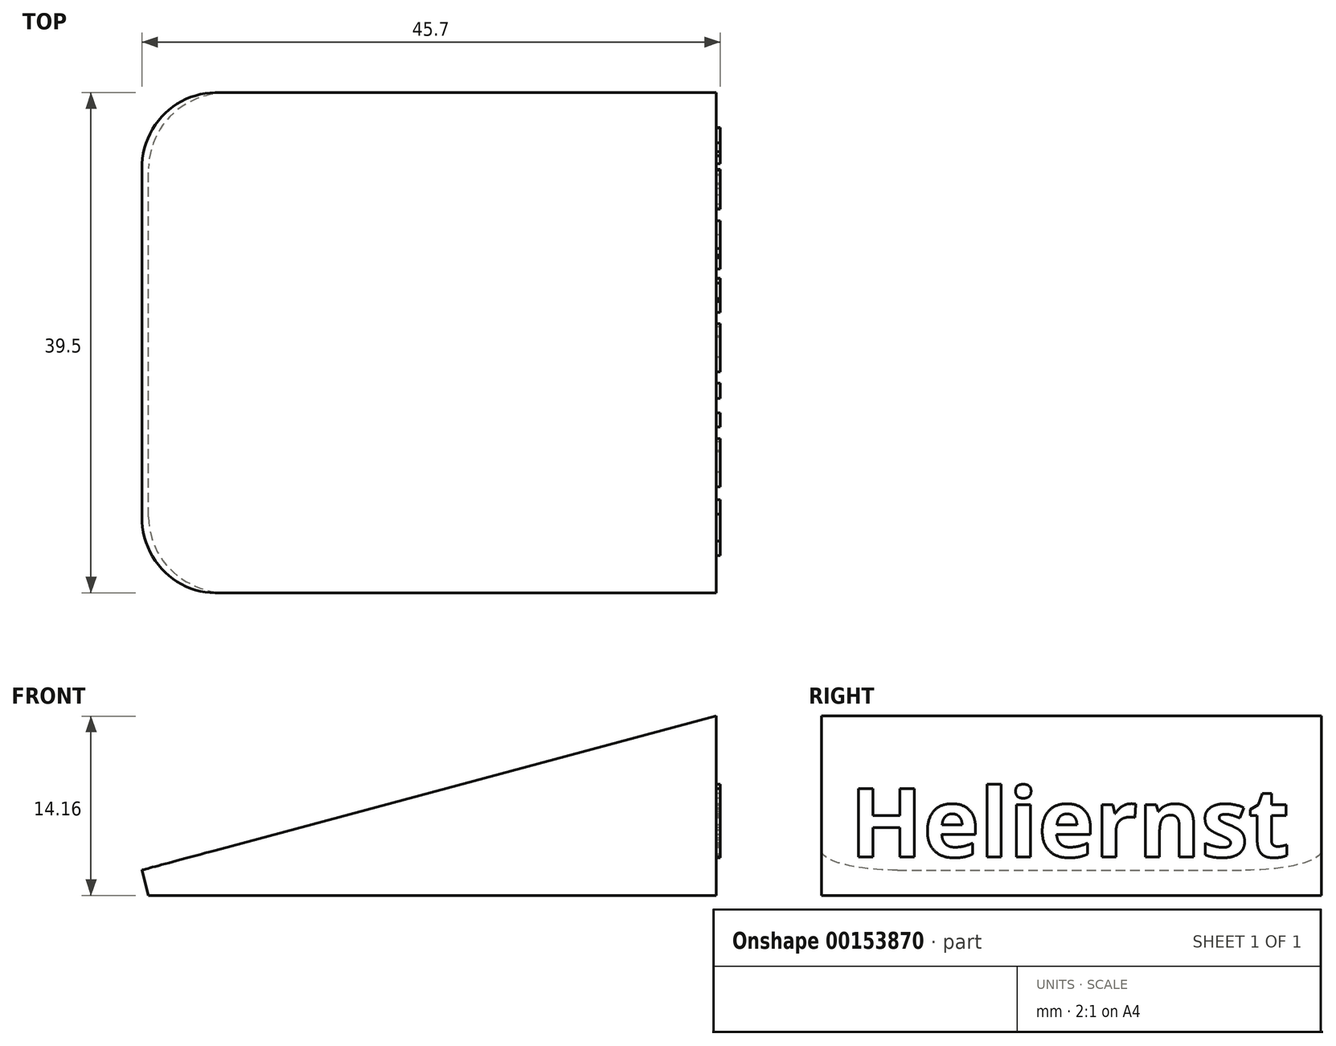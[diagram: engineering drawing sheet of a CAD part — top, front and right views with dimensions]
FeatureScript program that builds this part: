
annotation { "Feature Type Name" : "Feature", "Feature Type Description" : "" }
export const myFeature = defineFeature(function(context is Context, id is Id, definition is map)
    precondition{}
    {
        {
            var Q0;
            Q0=qCreatedBy(makeId("Right.planeOp"),FACE);
            var sketch = newSketch(context, id + "F0", { "sketchPlane" : qUnion([Q0])});
            skLineSegment(sketch, "E0", {"start": v(0, 0) * mm, "end": v(45.4, 0) * mm});
            skLineSegment(sketch, "E1", {"start": v(45.4, 0) * mm, "end": v(45.4, 14.16) * mm});
            skLineSegment(sketch, "E2", {"start": v(45.4, 14.16) * mm, "end": v(0, 2) * mm});
            skLineSegment(sketch, "E3", {"start": v(0, 2) * mm, "end": v(0, 0) * mm});
            skSolve(sketch);
        }
        {
            var Q0;
            Q0=qSketchRegion(id+"F0",true);
            extrude(context, id + "F1", {"entities" : qUnion([Q0]), "depth" : 39.5 * mm});
        }
        {
            var Q0;
            Q0=makeQuery(id+"F1.opExtrude","SWEPT_BODY",BODY,{"disambiguationData":[OSD([sQuery(id+"F0.wireOp",EDGE,"E0"),sQuery(id+"F0.wireOp",EDGE,"E1"),sQuery(id+"F0.wireOp",EDGE,"E2")])]});
            transform(context, id + "F2", {"entities" : qUnion([Q0]), "transformType" : TransformType.TRANSLATION_3D, "dx" : -10.75 * mm, "dy" : -78 * mm, "dz" : 41.5 * mm, "makeCopy" : true});
        }
        {
            var Q0;
            Q0=makeQuery(id+"F2.opPattern","COPY",BODY,{"derivedFrom":makeQuery(id+"F1.opExtrude","SWEPT_BODY",BODY,{"disambiguationData":[OSD([sQuery(id+"F0.wireOp",EDGE,"E0"),sQuery(id+"F0.wireOp",EDGE,"E1"),sQuery(id+"F0.wireOp",EDGE,"E2")])]}),"instanceName":"1"});
            deleteBodies(context, id + "F3", {"entities" : qUnion([Q0])});
        }
        {
            var Q0;
            Q0=makeQuery(id+"F1.opExtrude","SWEPT_BODY",BODY,{"disambiguationData":[OSD([sQuery(id+"F0.wireOp",EDGE,"E0"),sQuery(id+"F0.wireOp",EDGE,"E1"),sQuery(id+"F0.wireOp",EDGE,"E2")])]});
            var Q1;
            Q1=makeQuery(id+"F1.opExtrude","CAP_EDGE",EDGE,{"disambiguationData":[OSD([sQuery(id+"F0.wireOp",EDGE,"E1")])],"isStart":true});
            transform(context, id + "F4", {"entities" : qUnion([Q0]), "transformType" : TransformType.ROTATION, "transformAxis" : qUnion([Q1]), "angle" : 90 * degree, "makeCopy" : false});
        }
        {
            var Q0;
            Q0=makeQuery(id+"F1.opExtrude","SWEPT_BODY",BODY,{"disambiguationData":[OSD([sQuery(id+"F0.wireOp",EDGE,"E0"),sQuery(id+"F0.wireOp",EDGE,"E1"),sQuery(id+"F0.wireOp",EDGE,"E2")])]});
            var Q1;
            Q1=makeQuery(id+"F1.opExtrude","CAP_EDGE",EDGE,{"disambiguationData":[OSD([sQuery(id+"F0.wireOp",EDGE,"E1")])],"isStart":true});
            transform(context, id + "F5", {"entities" : qUnion([Q0]), "transformType" : TransformType.ROTATION, "transformAxis" : qUnion([Q1]), "angle" : 180 * degree, "makeCopy" : false});
        }
        {
            var Q0;
            Q0=makeQuery(id+"F1.opExtrude","SWEPT_FACE",FACE,{"disambiguationData":[OSD([sQuery(id+"F0.wireOp",EDGE,"E1")])]});
            var sketch = newSketch(context, id + "F6", { "sketchPlane" : qUnion([Q0])});
            skText(sketch, "E4", { "text": "Heliernst", "fontName": "OpenSans-Bold.ttf"});
            skLineSegment(sketch, "E5", {"start": v(25.65, 14.16) * mm, "end": v(25.65, -4.48) * mm, "construction": true});
            const initialGuessF6  = {"E4": [0.00815, 0.00304, 1, 0, 0.00544]};
            skSetInitialGuess(sketch, initialGuessF6);
            skSolve(sketch);
        }
        {
            var Q0;
            Q0 = qSketchRegion(id + "F6", true);
            extrude(context, id + "F7", {"entities" : qUnion([Q0]), "operationType" : NewBodyOperationType.ADD, "depth" : 0.3 * mm});
        }
        {
            var Q0;
            Q0=makeQuery(id+"F1.opExtrude","SWEPT_FACE",FACE,{"disambiguationData":[OSD([sQuery(id+"F0.wireOp",EDGE,"E2")])]});
            var sketch = newSketch(context, id + "F8", { "sketchPlane" : qUnion([Q0])});
            skLineSegment(sketch, "E6.bottom", {"start": v(-37.33, 45.4) * mm, "end": v(-34.83, 45.4) * mm});
            skLineSegment(sketch, "E6.top", {"start": v(-37.33, 5.9) * mm, "end": v(-34.83, 5.9) * mm});
            skLineSegment(sketch, "E6.left", {"start": v(-43.33, 39.4) * mm, "end": v(-43.33, 11.9) * mm});
            skLineSegment(sketch, "E6.right", {"start": v(-34.83, 45.4) * mm, "end": v(-34.83, 5.9) * mm});
            skPoint(sketch, "E7.visualSharp", {"position": v(-43.33, 45.4) * mm});
            skArc(sketch, "E7.filletArc", {"start": v(-37.33, 45.4) * mm, "mid": v(-41.58, 43.64) * mm, "end": v(-43.33, 39.4) * mm});
            skPoint(sketch, "E8.visualSharp", {"position": v(-43.33, 5.9) * mm});
            skArc(sketch, "E8.filletArc", {"start": v(-43.33, 11.9) * mm, "mid": v(-41.58, 7.66) * mm, "end": v(-37.33, 5.9) * mm});
            skSolve(sketch);
        }
        {
            var Q0;
            {var subQ0=sQuery(id+"F8.wireOp",EDGE,"E7.filletArc");Q0=makeQuery(id+"F8.imprint","IMPRINT",FACE,{"disambiguationData":[TD([[makeQuery(id+"F8.imprint","IMPRINT",EDGE,{"derivedFrom":subQ0}),-1.0]])]});}
            var Q1;
            Q1=makeQuery(id+"F1.opExtrude","SWEPT_FACE",FACE,{"disambiguationData":[OSD([sQuery(id+"F0.wireOp",EDGE,"E3")])]});
            var Q2;
            {var subQ0=sQuery(id+"F8.wireOp",EDGE,"E8.filletArc");Q2=makeQuery(id+"F8.imprint","IMPRINT",FACE,{"disambiguationData":[TD([[makeQuery(id+"F8.imprint","IMPRINT",EDGE,{"derivedFrom":subQ0}),-1.0]])]});}
            extrude(context, id + "F9", {"entities" : qUnion([Q0, Q1, Q2]), "operationType" : NewBodyOperationType.REMOVE, "endBound" : BoundingType.THROUGH_ALL, "oppositeDirection" : true, "depth" : 25 * mm});
        }
    });
